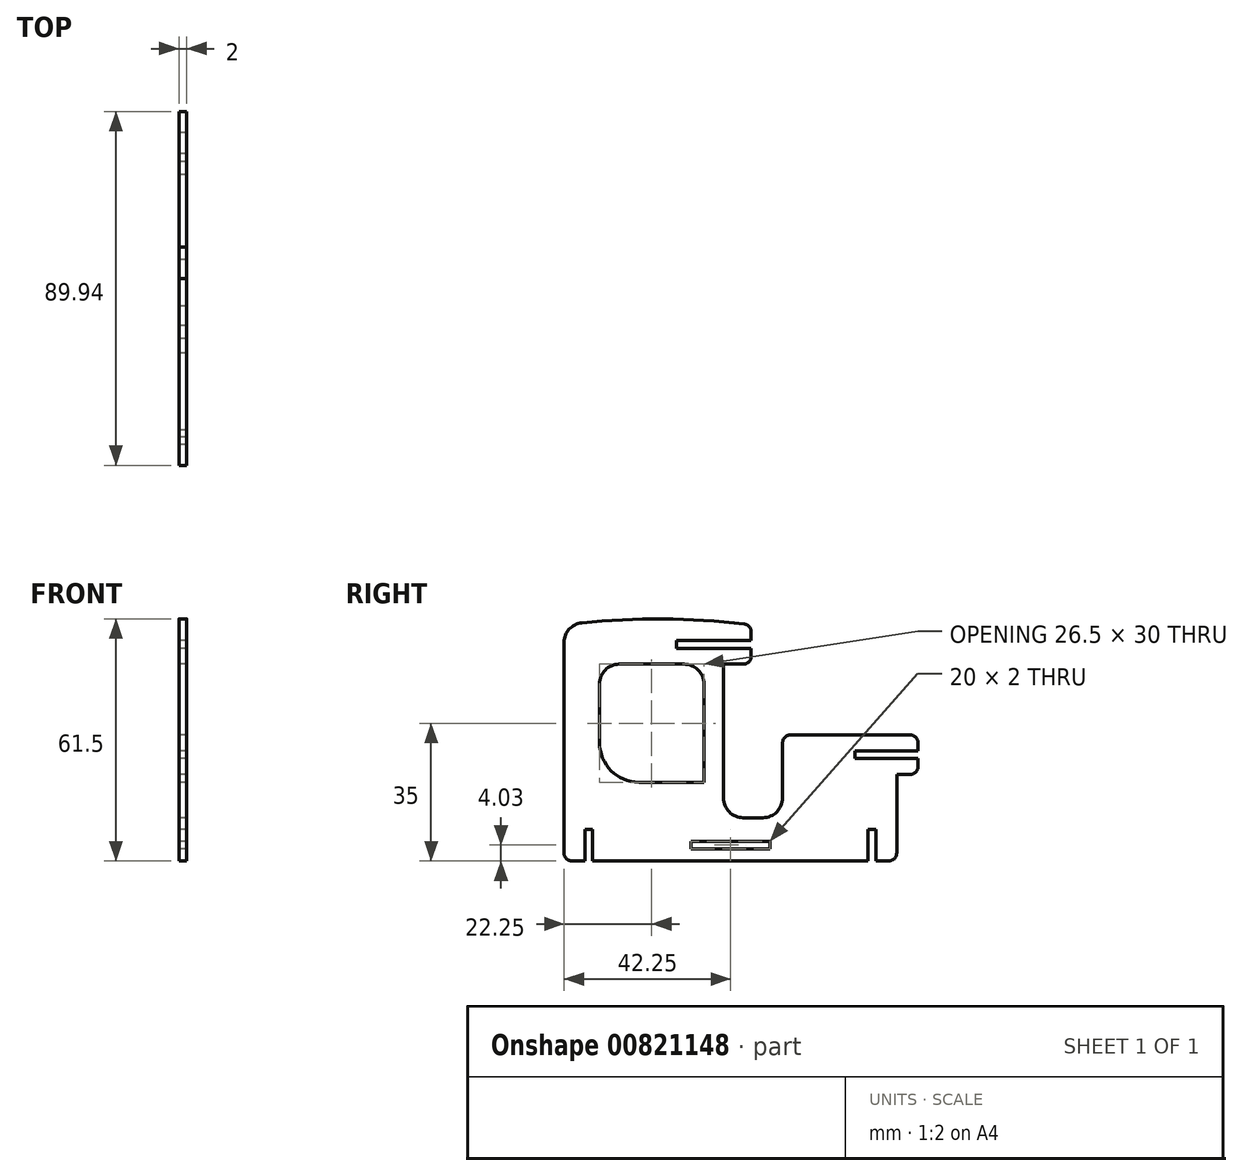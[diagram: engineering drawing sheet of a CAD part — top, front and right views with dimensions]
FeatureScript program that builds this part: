
annotation { "Feature Type Name" : "Feature", "Feature Type Description" : "" }
export const myFeature = defineFeature(function(context is Context, id is Id, definition is map)
    precondition{}
    {
        {
            var Q0;
            Q0=qCreatedBy(makeId("Right.planeOp"),FACE);
            var sketch = newSketch(context, id + "F0", { "sketchPlane" : qUnion([Q0])});
            skLineSegment(sketch, "E0.bottom", {"start": v(-21.75, -30) * mm, "end": v(-18.5, -30) * mm});
            skLineSegment(sketch, "E0.left", {"start": v(-23.75, -28) * mm, "end": v(-23.75, 25.54) * mm});
            skLineSegment(sketch, "E0.right", {"start": v(23.75, 22) * mm, "end": v(23.75, 24) * mm});
            skPoint(sketch, "E0.middle", {"position": v(0, 0) * mm});
            skPoint(sketch, "E1.endSnap0", {"position": v(-23.75, 0) * mm});
            skLineSegment(sketch, "E2", {"start": v(16.75, 20) * mm, "end": v(16.75, -14) * mm});
            skLineSegment(sketch, "E3", {"start": v(-9.75, 20) * mm, "end": v(6.75, 20) * mm});
            skLineSegment(sketch, "E4", {"start": v(23.75, -30) * mm, "end": v(53.5, -30) * mm});
            skLineSegment(sketch, "E5", {"start": v(21.75, -19) * mm, "end": v(26.75, -19) * mm});
            skLineSegment(sketch, "E6", {"start": v(33.75, 2) * mm, "end": v(64.19, 2) * mm});
            skLineSegment(sketch, "E7", {"start": v(31.75, 0) * mm, "end": v(31.75, -14) * mm});
            skPoint(sketch, "E7.endSnap0", {"position": v(32.25, -19) * mm});
            skPoint(sketch, "E8.orphan", {"position": v(47.75, -19) * mm});
            skLineSegment(sketch, "E9", {"start": v(60.75, -28) * mm, "end": v(60.75, -8) * mm});
            skLineSegment(sketch, "E10", {"start": v(60.75, -8) * mm, "end": v(64.19, -8) * mm});
            skLineSegment(sketch, "E11", {"start": v(66.19, 0) * mm, "end": v(66.19, -2) * mm});
            skLineSegment(sketch, "E12", {"start": v(66.19, -2) * mm, "end": v(50.19, -2) * mm});
            skLineSegment(sketch, "E13", {"start": v(66.19, -4) * mm, "end": v(50.19, -4) * mm});
            skLineSegment(sketch, "E14", {"start": v(50.19, -4) * mm, "end": v(50.19, -2) * mm});
            skPoint(sketch, "E15.end.orphan", {"position": v(50.19, -2.5) * mm});
            skPoint(sketch, "E15.start.orphan", {"position": v(66.19, -3) * mm});
            skLineSegment(sketch, "E16.trimOffspring", {"start": v(66.19, -4) * mm, "end": v(66.19, -6) * mm});
            skLineSegment(sketch, "E17", {"start": v(11.75, 15) * mm, "end": v(11.75, -10) * mm});
            skLineSegment(sketch, "E18", {"start": v(-14.75, 15) * mm, "end": v(-14.75, 0) * mm});
            skLineSegment(sketch, "E19.trimOffspring", {"start": v(16.75, 20) * mm, "end": v(21.75, 20) * mm});
            skLineSegment(sketch, "E20", {"start": v(-4.75, -10) * mm, "end": v(11.75, -10) * mm});
            skLineSegment(sketch, "E21", {"start": v(23.75, 24) * mm, "end": v(4.75, 24) * mm});
            skLineSegment(sketch, "E22", {"start": v(23.75, 26) * mm, "end": v(4.75, 26) * mm});
            skLineSegment(sketch, "E23", {"start": v(4.75, 24) * mm, "end": v(4.75, 26) * mm});
            skPoint(sketch, "E24.end.orphan", {"position": v(4.75, 25) * mm});
            skPoint(sketch, "E24.start.orphan", {"position": v(23.75, 25) * mm});
            skLineSegment(sketch, "E25.trimOffspring", {"start": v(23.75, 26) * mm, "end": v(23.75, 28.23) * mm});
            skPoint(sketch, "E26", {"position": v(0, 31.5) * mm});
            skPoint(sketch, "E26.positionSnap0", {"position": v(0, 30) * mm});
            skArc(sketch, "E27", {"start": v(21.98, 30.22) * mm, "mid": v(1.37, 31.5) * mm, "end": v(-19.26, 30.51) * mm});
            skPoint(sketch, "E28.visualSharp", {"position": v(23.75, 30) * mm});
            skArc(sketch, "E28.filletArc", {"start": v(23.75, 28.23) * mm, "mid": v(23.24, 29.56) * mm, "end": v(21.98, 30.22) * mm});
            skPoint(sketch, "E29.visualSharp", {"position": v(-23.75, 30) * mm});
            skArc(sketch, "E29.filletArc", {"start": v(-19.26, 30.51) * mm, "mid": v(-22.46, 28.9) * mm, "end": v(-23.75, 25.54) * mm});
            skPoint(sketch, "E30.visualSharp", {"position": v(-14.75, 20) * mm});
            skArc(sketch, "E30.filletArc", {"start": v(-9.75, 20) * mm, "mid": v(-13.29, 18.54) * mm, "end": v(-14.75, 15) * mm});
            skPoint(sketch, "E31.visualSharp", {"position": v(-14.75, -10) * mm});
            skArc(sketch, "E31.filletArc", {"start": v(-14.75, 0) * mm, "mid": v(-11.82, -7.07) * mm, "end": v(-4.75, -10) * mm});
            skPoint(sketch, "E32.visualSharp", {"position": v(11.75, 20) * mm});
            skArc(sketch, "E32.filletArc", {"start": v(11.75, 15) * mm, "mid": v(10.29, 18.54) * mm, "end": v(6.75, 20) * mm});
            skPoint(sketch, "E33.visualSharp", {"position": v(16.75, -19) * mm});
            skArc(sketch, "E33.filletArc", {"start": v(16.75, -14) * mm, "mid": v(18.21, -17.54) * mm, "end": v(21.75, -19) * mm});
            skPoint(sketch, "E34.newPointB", {"position": v(31.75, -19) * mm});
            skArc(sketch, "E34.filletArc", {"start": v(26.75, -19) * mm, "mid": v(30.29, -17.54) * mm, "end": v(31.75, -14) * mm});
            skPoint(sketch, "E35.visualSharp", {"position": v(23.75, 20) * mm});
            skArc(sketch, "E35.filletArc", {"start": v(21.75, 20) * mm, "mid": v(23.16, 20.59) * mm, "end": v(23.75, 22) * mm});
            skPoint(sketch, "E36.visualSharp", {"position": v(31.75, 2) * mm});
            skArc(sketch, "E36.filletArc", {"start": v(33.75, 2) * mm, "mid": v(32.34, 1.41) * mm, "end": v(31.75, 0) * mm});
            skPoint(sketch, "E37.visualSharp", {"position": v(66.19, 2) * mm});
            skArc(sketch, "E37.filletArc", {"start": v(66.19, 0) * mm, "mid": v(65.6, 1.41) * mm, "end": v(64.19, 2) * mm});
            skPoint(sketch, "E38.visualSharp", {"position": v(66.19, -8) * mm});
            skArc(sketch, "E38.filletArc", {"start": v(64.19, -8) * mm, "mid": v(65.6, -7.41) * mm, "end": v(66.19, -6) * mm});
            skLineSegment(sketch, "E39", {"start": v(-18.5, -30) * mm, "end": v(-18.5, -22) * mm});
            skLineSegment(sketch, "E40", {"start": v(-18.5, -22) * mm, "end": v(-16.5, -22) * mm});
            skLineSegment(sketch, "E41", {"start": v(-16.5, -22) * mm, "end": v(-16.5, -30) * mm});
            skPoint(sketch, "E42.orphan", {"position": v(-14.5, -22) * mm});
            skLineSegment(sketch, "E43.trimOffspring", {"start": v(-16.5, -30) * mm, "end": v(23.75, -30) * mm});
            skLineSegment(sketch, "E44", {"start": v(55.5, -30) * mm, "end": v(55.5, -22) * mm});
            skLineSegment(sketch, "E45", {"start": v(53.5, -30) * mm, "end": v(53.5, -22) * mm});
            skLineSegment(sketch, "E46", {"start": v(53.5, -22) * mm, "end": v(55.5, -22) * mm});
            skLineSegment(sketch, "E47.trimOffspring", {"start": v(55.5, -30) * mm, "end": v(58.75, -30) * mm});
            skPoint(sketch, "E48.visualSharp", {"position": v(-23.75, -30) * mm});
            skArc(sketch, "E48.filletArc", {"start": v(-23.75, -28) * mm, "mid": v(-23.16, -29.41) * mm, "end": v(-21.75, -30) * mm});
            skPoint(sketch, "E49.visualSharp", {"position": v(60.75, -30) * mm});
            skArc(sketch, "E49.filletArc", {"start": v(58.75, -30) * mm, "mid": v(60.16, -29.41) * mm, "end": v(60.75, -28) * mm});
            skLineSegment(sketch, "E50.bottom", {"start": v(28.5, -26.97) * mm, "end": v(8.5, -26.97) * mm});
            skLineSegment(sketch, "E50.top", {"start": v(28.5, -24.97) * mm, "end": v(8.5, -24.97) * mm});
            skLineSegment(sketch, "E50.left", {"start": v(28.5, -26.97) * mm, "end": v(28.5, -24.97) * mm});
            skLineSegment(sketch, "E50.right", {"start": v(8.5, -26.97) * mm, "end": v(8.5, -24.97) * mm});
            skPoint(sketch, "E50.middle", {"position": v(18.5, -25.97) * mm});
            skSolve(sketch);
        }
        {
            var Q0;
            Q0 = qSketchRegion(id + "F0", true);
            extrude(context, id + "F1", {"entities" : qUnion([Q0]), "depth" : 2 * mm, "offsetDistance" : 25 * mm});
        }
    });
